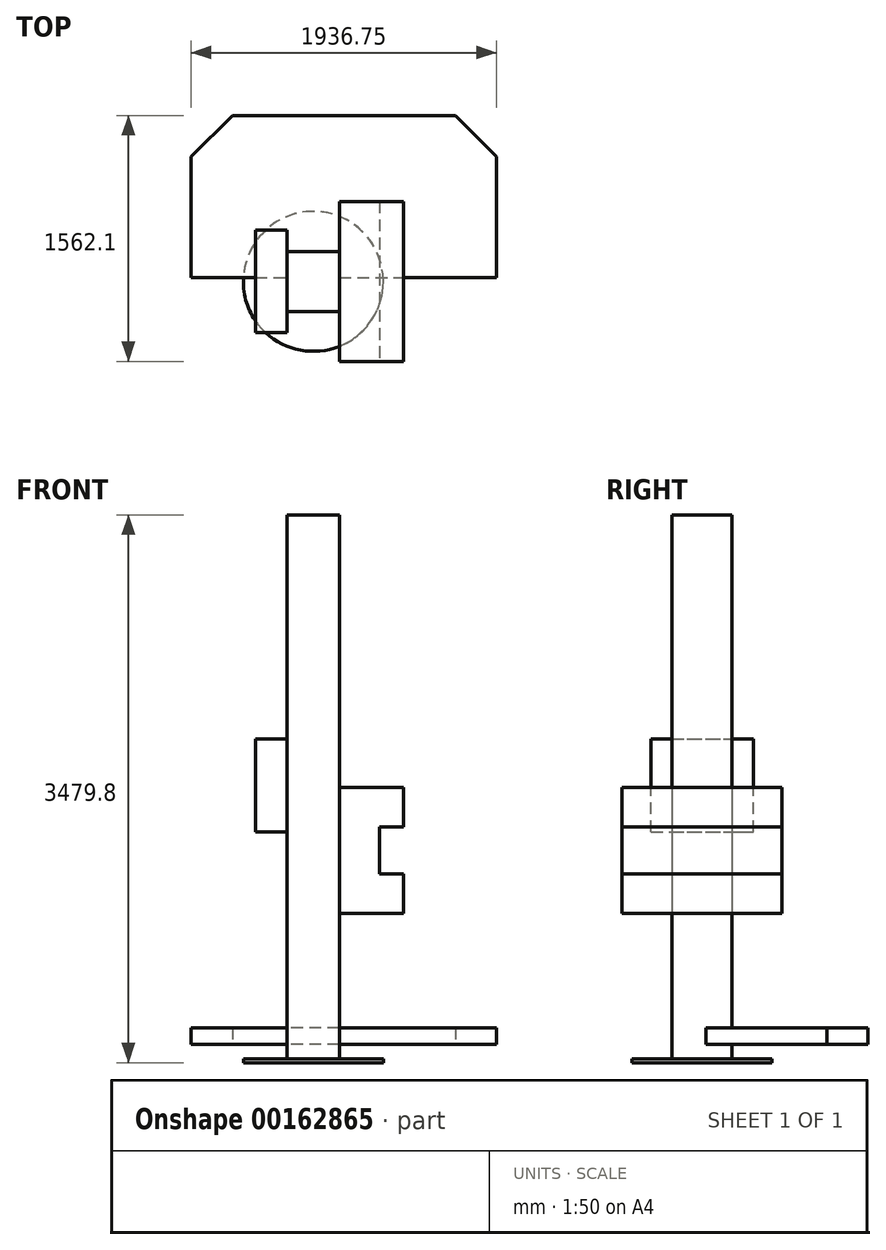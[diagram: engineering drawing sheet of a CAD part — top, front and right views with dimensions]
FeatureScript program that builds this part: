
annotation { "Feature Type Name" : "Feature", "Feature Type Description" : "" }
export const myFeature = defineFeature(function(context is Context, id is Id, definition is map)
    precondition{}
    {
        {
            var Q0;
            Q0=qCreatedBy(makeId("Top.planeOp"),FACE);
            var sketch = newSketch(context, id + "F0", { "sketchPlane" : qUnion([Q0])});
            skCircle(sketch, "E0", {"center": v(0, 0) * mm, "radius": 444.5 * mm});
            skSolve(sketch);
        }
        {
            var Q0;
            Q0=makeQuery(id+"F0.imprint","IMPRINT",FACE,{"disambiguationData":[TD([[makeQuery(id+"F0.imprint","IMPRINT",EDGE,{"derivedFrom":sQuery(id+"F0.wireOp",EDGE,"E0")}),1.0]])]});
            extrude(context, id + "F1", {"entities" : qUnion([Q0]), "depth" : 25.4 * mm});
        }
        {
            var Q0;
            Q0=makeQuery(id+"F1.opExtrude","CAP_FACE",FACE,{"disambiguationData":[OSD([sQuery(id+"F0.wireOp",EDGE,"E0")])],"isStart":false});
            var sketch = newSketch(context, id + "F2", { "sketchPlane" : qUnion([Q0])});
            skLineSegment(sketch, "E1.bottom", {"start": v(165.1, -190.5) * mm, "end": v(-165.1, -190.5) * mm});
            skLineSegment(sketch, "E1.top", {"start": v(165.1, 190.5) * mm, "end": v(-165.1, 190.5) * mm});
            skLineSegment(sketch, "E1.left", {"start": v(165.1, -190.5) * mm, "end": v(165.1, 190.5) * mm});
            skLineSegment(sketch, "E1.right", {"start": v(-165.1, -190.5) * mm, "end": v(-165.1, 190.5) * mm});
            skPoint(sketch, "E1.middle", {"position": v(0, 0) * mm});
            skSolve(sketch);
        }
        {
            var Q0;
            Q0=makeQuery(id+"F2.imprint","IMPRINT",FACE,{"disambiguationData":[TD([[makeQuery(id+"F2.imprint","IMPRINT",EDGE,{"derivedFrom":sQuery(id+"F2.wireOp",EDGE,"E1.bottom")}),-1.0]])]});
            extrude(context, id + "F3", {"entities" : qUnion([Q0]), "operationType" : NewBodyOperationType.ADD, "depth" : 3454.4 * mm});
        }
        {
            var Q0;
            Q0=makeQuery(id+"F1.opExtrude","CAP_FACE",FACE,{"disambiguationData":[OSD([sQuery(id+"F0.wireOp",EDGE,"E0")])],"isStart":false});
            cPlane(context, id + "F4", {"entities" : qUnion([Q0]), "cplaneType" : CPlaneType.OFFSET, "offset" : 92.07 * mm, "width" : 152.4 * mm, "height" : 152.4 * mm});
        }
        {
            var Q0;
            Q0=qCreatedBy(id+"F4.planeOp",FACE);
            var sketch = newSketch(context, id + "F5", { "sketchPlane" : qUnion([Q0])});
            skLineSegment(sketch, "E2", {"start": v(0, 25.4) * mm, "end": v(1162.05, 25.4) * mm});
            skLineSegment(sketch, "E3", {"start": v(1162.05, 25.4) * mm, "end": v(1162.05, 1041.4) * mm});
            skLineSegment(sketch, "E4", {"start": v(0, 25.4) * mm, "end": v(-774.7, 25.4) * mm});
            skLineSegment(sketch, "E5", {"start": v(-774.7, 25.4) * mm, "end": v(-774.7, 793.75) * mm});
            skLineSegment(sketch, "E6", {"start": v(-774.7, 793.75) * mm, "end": v(-514.35, 793.75) * mm});
            skLineSegment(sketch, "E7", {"start": v(-514.35, 793.75) * mm, "end": v(-514.35, 1054.1) * mm});
            skLineSegment(sketch, "E8", {"start": v(-514.35, 1054.1) * mm, "end": v(901.7, 1054.1) * mm});
            skLineSegment(sketch, "E9", {"start": v(901.7, 1054.1) * mm, "end": v(901.7, 793.75) * mm});
            skLineSegment(sketch, "E10", {"start": v(901.7, 793.75) * mm, "end": v(1162.05, 793.75) * mm});
            skLineSegment(sketch, "E11", {"start": v(-774.7, 793.75) * mm, "end": v(-514.35, 1054.1) * mm});
            skLineSegment(sketch, "E12", {"start": v(901.7, 1054.1) * mm, "end": v(1162.05, 793.75) * mm});
            skSolve(sketch);
        }
        {
            var Q0;
            {var subQ1=sQuery(id+"F5.wireOp",EDGE,"E2");Q0=makeQuery(id+"F5.imprint","IMPRINT",FACE,{"disambiguationData":[TD([[makeQuery(id+"F5.imprint","IMPRINT",EDGE,{"derivedFrom":subQ1}),1.0]])]});}
            var Q1;
            Q1=makeQuery(id+"F5.imprint","IMPRINT",FACE,{"disambiguationData":[TD([[makeQuery(id+"F5.imprint","IMPRINT",EDGE,{"derivedFrom":sQuery(id+"F5.wireOp",EDGE,"E9")}),1.0]])]});
            var Q2;
            Q2=makeQuery(id+"F5.imprint","IMPRINT",FACE,{"disambiguationData":[TD([[makeQuery(id+"F5.imprint","IMPRINT",EDGE,{"derivedFrom":sQuery(id+"F5.wireOp",EDGE,"E6")}),1.0]])]});
            extrude(context, id + "F6", {"entities" : qUnion([Q0, Q1, Q2]), "operationType" : NewBodyOperationType.ADD, "depth" : 104.77 * mm});
        }
        {
            var Q0;
            Q0=makeQuery(id+"F3.opExtrude","SWEPT_FACE",FACE,{"disambiguationData":[OSD([sQuery(id+"F2.wireOp",EDGE,"E1.left")])]});
            var sketch = newSketch(context, id + "F7", { "sketchPlane" : qUnion([Q0])});
            skLineSegment(sketch, "E13.bottom", {"start": v(508, 947.74) * mm, "end": v(-508, 947.74) * mm});
            skLineSegment(sketch, "E13.top", {"start": v(508, 1747.84) * mm, "end": v(-508, 1747.84) * mm});
            skLineSegment(sketch, "E13.left", {"start": v(508, 947.74) * mm, "end": v(508, 1747.84) * mm});
            skLineSegment(sketch, "E13.right", {"start": v(-508, 947.74) * mm, "end": v(-508, 1747.84) * mm});
            skPoint(sketch, "E13.middle", {"position": v(0, 1347.79) * mm});
            skSolve(sketch);
        }
        {
            var Q0;
            {var subQ0=sQuery(id+"F7.wireOp",EDGE,"E13.bottom");var subQ1=sQuery(id+"F2.wireOp",EDGE,"E1.left");var subQ3=sQuery(id+"F2.wireOp",EDGE,"E1.bottom");var subQ6=makeQuery(id+"F3.opExtrude","SWEPT_EDGE",EDGE,{"disambiguationData":[OSD([subQ3,subQ1])]});var subQ7=makeQuery(id+"F7.imprint","INTERSECT",VERTEX,{"derivedFrom":[subQ6,subQ0]});Q0=makeQuery(id+"F7.imprint","IMPRINT",FACE,{"disambiguationData":[TD([[makeQuery(id+"F7.imprint","IMPRINT",EDGE,{"disambiguationData":[TD([[subQ7,1.0]])],"derivedFrom":subQ6}),1.0]])]});}
            var Q1;
            {var subQ0=sQuery(id+"F7.wireOp",EDGE,"E13.right");Q1=makeQuery(id+"F7.imprint","IMPRINT",FACE,{"disambiguationData":[TD([[makeQuery(id+"F7.imprint","IMPRINT",EDGE,{"derivedFrom":subQ0}),-1.0]])]});}
            var Q2;
            {var subQ0=sQuery(id+"F7.wireOp",EDGE,"E13.left");Q2=makeQuery(id+"F7.imprint","IMPRINT",FACE,{"disambiguationData":[TD([[makeQuery(id+"F7.imprint","IMPRINT",EDGE,{"derivedFrom":subQ0}),1.0]])]});}
            extrude(context, id + "F8", {"entities" : qUnion([Q0, Q1, Q2]), "operationType" : NewBodyOperationType.ADD, "depth" : 254 * mm});
        }
        {
            var Q0;
            Q0=makeQuery(id+"F8.opExtrude","CAP_FACE",FACE,{"disambiguationData":[OSD([sQuery(id+"F7.wireOp",EDGE,"E13.bottom"),sQuery(id+"F7.wireOp",EDGE,"E13.top"),sQuery(id+"F7.wireOp",EDGE,"E13.left"),sQuery(id+"F7.wireOp",EDGE,"E13.right")])],"isStart":false});
            var sketch = newSketch(context, id + "F9", { "sketchPlane" : qUnion([Q0])});
            skLineSegment(sketch, "E14.bottom", {"start": v(-508, 1747.84) * mm, "end": v(508, 1747.84) * mm});
            skLineSegment(sketch, "E14.top", {"start": v(-508, 947.74) * mm, "end": v(508, 947.74) * mm});
            skLineSegment(sketch, "E14.left", {"start": v(-508, 1747.84) * mm, "end": v(-508, 947.74) * mm});
            skLineSegment(sketch, "E14.right", {"start": v(508, 1747.84) * mm, "end": v(508, 947.74) * mm});
            skLineSegment(sketch, "E15", {"start": v(-508, 1497.01) * mm, "end": v(508, 1497.01) * mm});
            skLineSegment(sketch, "E16", {"start": v(508, 1198.56) * mm, "end": v(-508, 1198.56) * mm});
            skSolve(sketch);
        }
        {
            var Q0;
            {var subQ0=sQuery(id+"F9.wireOp",EDGE,"E14.bottom");Q0=makeQuery(id+"F9.imprint","IMPRINT",FACE,{"disambiguationData":[TD([[makeQuery(id+"F9.imprint","IMPRINT",EDGE,{"derivedFrom":subQ0}),1.0]])]});}
            var Q1;
            {var subQ0=sQuery(id+"F9.wireOp",EDGE,"E14.top");Q1=makeQuery(id+"F9.imprint","IMPRINT",FACE,{"disambiguationData":[TD([[makeQuery(id+"F9.imprint","IMPRINT",EDGE,{"derivedFrom":subQ0}),-1.0]])]});}
            extrude(context, id + "F10", {"entities" : qUnion([Q0, Q1]), "operationType" : NewBodyOperationType.ADD, "depth" : 152.4 * mm});
        }
        {
            var Q0;
            Q0=makeQuery(id+"F3.opExtrude","SWEPT_FACE",FACE,{"disambiguationData":[OSD([sQuery(id+"F2.wireOp",EDGE,"E1.right")])]});
            var sketch = newSketch(context, id + "F11", { "sketchPlane" : qUnion([Q0])});
            skLineSegment(sketch, "E17.bottom", {"start": v(325.6, 1464.43) * mm, "end": v(-325.6, 1464.43) * mm});
            skLineSegment(sketch, "E17.top", {"start": v(325.6, 2054.65) * mm, "end": v(-325.6, 2054.65) * mm});
            skLineSegment(sketch, "E17.left", {"start": v(325.6, 1464.43) * mm, "end": v(325.6, 2054.65) * mm});
            skLineSegment(sketch, "E17.right", {"start": v(-325.6, 1464.43) * mm, "end": v(-325.6, 2054.65) * mm});
            skPoint(sketch, "E17.middle", {"position": v(0, 1759.54) * mm});
            skPoint(sketch, "E17.middle.positionSnap0", {"position": v(0, 3479.8) * mm});
            skPoint(sketch, "E17.centerSnap0", {"position": v(0, 3479.8) * mm});
            skSolve(sketch);
        }
        {
            var Q0;
            Q0 = qSketchRegion(id + "F11", true);
            extrude(context, id + "F12", {"entities" : qUnion([Q0]), "operationType" : NewBodyOperationType.ADD, "depth" : 203.2 * mm});
        }
    });
